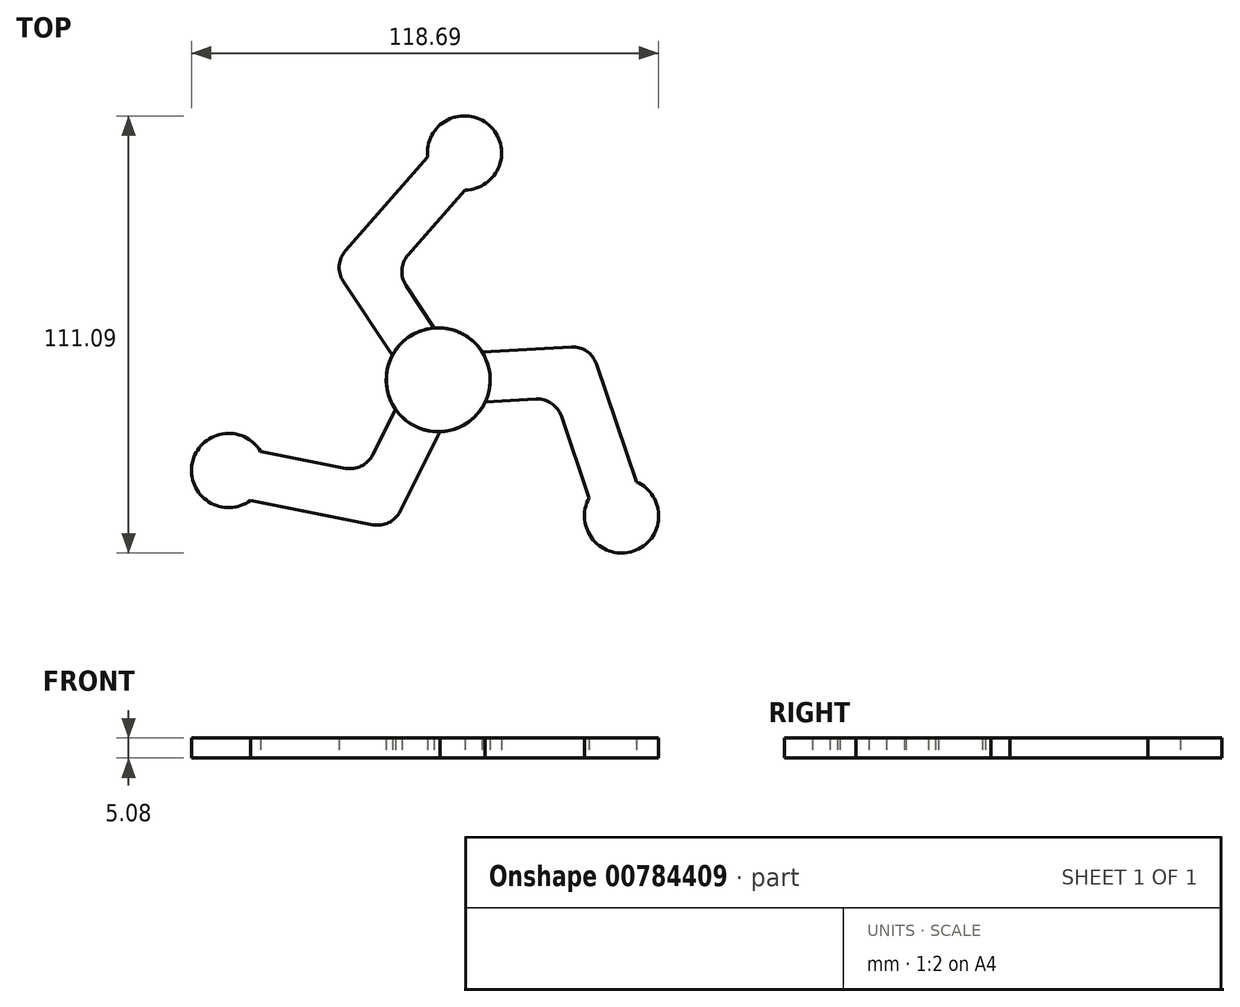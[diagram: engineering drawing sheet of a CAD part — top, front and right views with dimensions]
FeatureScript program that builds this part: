
annotation { "Feature Type Name" : "Feature", "Feature Type Description" : "" }
export const myFeature = defineFeature(function(context is Context, id is Id, definition is map)
    precondition{}
    {
        {
            var Q0;
            Q0=qCreatedBy(makeId("Top.planeOp"),FACE);
            var sketch = newSketch(context, id + "F0", { "sketchPlane" : qUnion([Q0])});
            skArc(sketch, "E0", {"start": v(6.84, 48.2) * mm, "mid": v(12.89, 64.73) * mm, "end": v(-2.7, 56.58) * mm});
            skArc(sketch, "E1", {"start": v(-11.66, 6.17) * mm, "mid": v(7.25, -11.02) * mm, "end": v(-1.05, 13.15) * mm});
            skLineSegment(sketch, "E2.0", {"start": v(-7.66, 31.68) * mm, "end": v(6.84, 48.2) * mm});
            skLineSegment(sketch, "E3.0", {"start": v(-23.59, 32.78) * mm, "end": v(-2.7, 56.58) * mm});
            skLineSegment(sketch, "E4.0", {"start": v(-1.05, 13.15) * mm, "end": v(-8.2, 24) * mm});
            skLineSegment(sketch, "E5.0", {"start": v(-11.66, 6.17) * mm, "end": v(-24.12, 25.1) * mm});
            skArc(sketch, "E6.filletArc", {"start": v(-7.66, 31.68) * mm, "mid": v(-9.22, 27.93) * mm, "end": v(-8.2, 24) * mm});
            skArc(sketch, "E7.filletArc", {"start": v(-23.59, 32.78) * mm, "mid": v(-25.15, 29.03) * mm, "end": v(-24.12, 25.1) * mm});
            skSolve(sketch);
        }
        {
            var Q0;
            Q0 = qSketchRegion(id + "F0", true);
            extrude(context, id + "F1", {"entities" : qUnion([Q0]), "depth" : 5.08 * mm, "offsetDistance" : 25.4 * mm});
        }
        {
            var Q0;
            Q0=qCreatedBy(makeId("Front.planeOp"),FACE);
            var sketch = newSketch(context, id + "F2", { "sketchPlane" : qUnion([Q0])});
            skLineSegment(sketch, "E8", {"start": v(0, 0) * mm, "end": v(0, 68.87) * mm});
            skSolve(sketch);
        }
        {
            var Q0;
            Q0=makeQuery(id+"F1.opExtrude","SWEPT_BODY",BODY,{"disambiguationData":[OSD([sQuery(id+"F0.wireOp",EDGE,"E0"),sQuery(id+"F0.wireOp",EDGE,"E1"),sQuery(id+"F0.wireOp",EDGE,"E2.0"),sQuery(id+"F0.wireOp",EDGE,"E3.0"),sQuery(id+"F0.wireOp",EDGE,"E4.0"),sQuery(id+"F0.wireOp",EDGE,"E5.0"),sQuery(id+"F0.wireOp",EDGE,"E6.filletArc"),sQuery(id+"F0.wireOp",EDGE,"E7.filletArc")])]});
            var Q1;
            Q1=sQuery(id+"F2.wireOp",EDGE,"E8");
            circularPattern(context, id + "F3", {"entities" : qUnion([Q0]), "axis" : qUnion([Q1]), "angle" : 360 * degree, "instanceCount" : 3, "equalSpace" : true});
        }
    });
